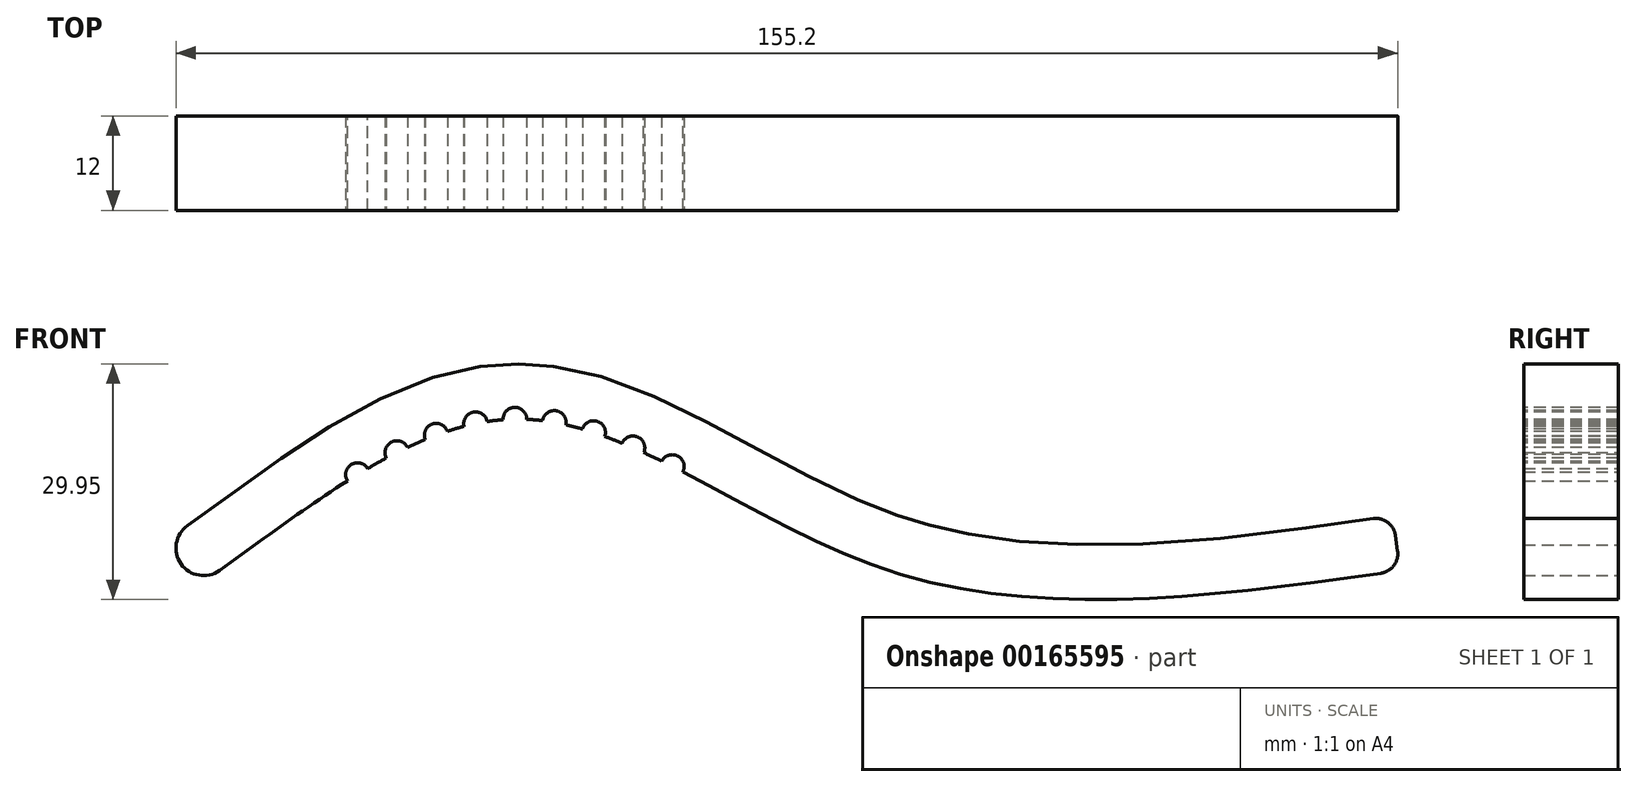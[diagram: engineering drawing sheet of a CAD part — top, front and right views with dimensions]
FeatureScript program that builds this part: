
annotation { "Feature Type Name" : "Feature", "Feature Type Description" : "" }
export const myFeature = defineFeature(function(context is Context, id is Id, definition is map)
    precondition{}
    {
        {
            var Q0;
            Q0=qCreatedBy(makeId("Front.planeOp"),FACE);
            var sketch = newSketch(context, id + "F0", { "sketchPlane" : qUnion([Q0])});
            skFitSpline(sketch, "E0", {"points": [v(0, 0) * mm, v(38.6, 19.22) * mm, v(85, 0) * mm, v(150, 0) * mm], "startDerivative": vector(125.86, 89.11) * mm, "endDerivative": vector(182.2, 25.52) * mm});
            skFitSpline(sketch, "E1.0", {"points": [v(-4.04, 5.71) * mm, v(-1.49, 7.52) * mm, v(2.43, 10.4) * mm, v(7.83, 14.23) * mm, v(11.99, 17) * mm, v(16.26, 19.61) * mm, v(20.7, 21.96) * mm, v(25.3, 23.93) * mm, v(29.34, 25.16) * mm, v(32.68, 25.83) * mm, v(35.24, 26.15) * mm, v(37.42, 26.25) * mm, v(39.19, 26.21) * mm, v(40.94, 26.1) * mm, v(43.1, 25.84) * mm, v(46.47, 25.18) * mm, v(50.55, 23.97) * mm, v(55.28, 22.08) * mm, v(59.88, 19.9) * mm, v(64.4, 17.54) * mm, v(68.9, 15.11) * mm, v(73.35, 12.73) * mm, v(77.8, 10.47) * mm, v(81.5, 8.8) * mm, v(84.44, 7.6) * mm, v(86.28, 6.94) * mm, v(87.75, 6.46) * mm, v(89.24, 6.01) * mm, v(91.12, 5.5) * mm, v(93.42, 4.97) * mm, v(96.54, 4.37) * mm, v(100.54, 3.8) * mm, v(105.5, 3.4) * mm, v(110.6, 3.27) * mm, v(117.56, 3.38) * mm, v(126.55, 4.02) * mm, v(137.67, 5.34) * mm, v(145.23, 6.4) * mm, v(149.03, 6.93) * mm]});
            skLineSegment(sketch, "E2", {"start": v(149.03, 6.93) * mm, "end": v(150, 0) * mm});
            skArc(sketch, "E3", {"start": v(-4.04, 5.71) * mm, "mid": v(-4.88, 0.83) * mm, "end": v(0, 0) * mm});
            skSolve(sketch);
        }
        {
            var Q0;
            Q0=qSketchRegion(id+"F0",true);
            extrude(context, id + "F1", {"entities" : qUnion([Q0]), "endBound" : BoundingType.SYMMETRIC, "depth" : 12 * mm});
        }
        {
            var Q0;
            Q0=makeQuery(id+"F1.opExtrude","SWEPT_EDGE",EDGE,{"disambiguationData":[OSD([sQuery(id+"F0.wireOp",EDGE,"E1.0"),sQuery(id+"F0.wireOp",EDGE,"6Faxudxn-1uMk-8ccC-NPzW-HdiGVZOxfaOw")])]});
            var Q1;
            Q1=makeQuery(id+"F1.opExtrude","SWEPT_EDGE",EDGE,{"disambiguationData":[OSD([sQuery(id+"F0.wireOp",EDGE,"E0"),sQuery(id+"F0.wireOp",EDGE,"6Faxudxn-1uMk-8ccC-NPzW-HdiGVZOxfaOw")])]});
            fillet(context, id + "F2", {"entities" : qUnion([Q0, Q1]), "radius" : 2.5 * mm, "tangentPropagation" : true, "allowEdgeOverflow" : false});
        }
        {
            var Q0;
            Q0=makeQuery(id+"F1.opExtrude","CAP_FACE",FACE,{"disambiguationData":[OSD([sQuery(id+"F0.wireOp",EDGE,"E0"),sQuery(id+"F0.wireOp",EDGE,"E1.0"),sQuery(id+"F0.wireOp",EDGE,"E2"),sQuery(id+"F0.wireOp",EDGE,"E3")])],"isStart":false});
            var sketch = newSketch(context, id + "F3", { "sketchPlane" : qUnion([Q0])});
            skCircle(sketch, "E4", {"center": v(37.53, 19.22) * mm, "radius": 1.5 * mm});
            skCircle(sketch, "E5", {"center": v(32.53, 18.65) * mm, "radius": 1.5 * mm});
            skCircle(sketch, "E6", {"center": v(27.53, 17.2) * mm, "radius": 1.5 * mm});
            skCircle(sketch, "E7", {"center": v(22.53, 14.98) * mm, "radius": 1.5 * mm});
            skCircle(sketch, "E8", {"center": v(17.53, 12.18) * mm, "radius": 1.5 * mm});
            skCircle(sketch, "E9", {"center": v(42.53, 18.8) * mm, "radius": 1.5 * mm});
            skCircle(sketch, "E10", {"center": v(47.53, 17.52) * mm, "radius": 1.5 * mm});
            skCircle(sketch, "E11", {"center": v(52.53, 15.58) * mm, "radius": 1.5 * mm});
            skCircle(sketch, "E12", {"center": v(57.53, 13.21) * mm, "radius": 1.5 * mm});
            skSolve(sketch);
        }
        {
            var Q0;
            Q0=qSketchRegion(id+"F3",true);
            extrude(context, id + "F4", {"entities" : qUnion([Q0]), "operationType" : NewBodyOperationType.REMOVE, "endBound" : BoundingType.THROUGH_ALL, "oppositeDirection" : true, "depth" : 25 * mm});
        }
        {
            var Q0;
            Q0=makeQuery(id+"F1.opExtrude","SWEPT_BODY",BODY,{"disambiguationData":[OSD([sQuery(id+"F0.wireOp",EDGE,"E0"),sQuery(id+"F0.wireOp",EDGE,"E1.0"),sQuery(id+"F0.wireOp",EDGE,"E2"),sQuery(id+"F0.wireOp",EDGE,"E3")])]});
            transform(context, id + "F5", {"entities" : qUnion([Q0]), "transformType" : TransformType.TRANSLATION_3D, "dx" : 0 * mm, "dy" : 0 * mm, "dz" : 0 * mm, "makeCopy" : true});
        }
        {
            var Q0;
            Q0=makeQuery(id+"F1.opExtrude","SWEPT_BODY",BODY,{"disambiguationData":[OSD([sQuery(id+"F0.wireOp",EDGE,"E0"),sQuery(id+"F0.wireOp",EDGE,"E1.0"),sQuery(id+"F0.wireOp",EDGE,"E2"),sQuery(id+"F0.wireOp",EDGE,"E3")])]});
            transform(context, id + "F6", {"entities" : qUnion([Q0]), "transformType" : TransformType.TRANSLATION_3D, "dx" : 0 * mm, "dy" : 0 * mm, "dz" : 0 * mm, "makeCopy" : true});
        }
        {
            var Q0;
            Q0=makeQuery(id+"F5.opPattern","COPY",BODY,{"derivedFrom":makeQuery(id+"F1.opExtrude","SWEPT_BODY",BODY,{"disambiguationData":[OSD([sQuery(id+"F0.wireOp",EDGE,"E0"),sQuery(id+"F0.wireOp",EDGE,"E1.0"),sQuery(id+"F0.wireOp",EDGE,"E2"),sQuery(id+"F0.wireOp",EDGE,"E3")])]}),"instanceName":"1"});
            deleteBodies(context, id + "F7", {"entities" : qUnion([Q0])});
        }
    });
